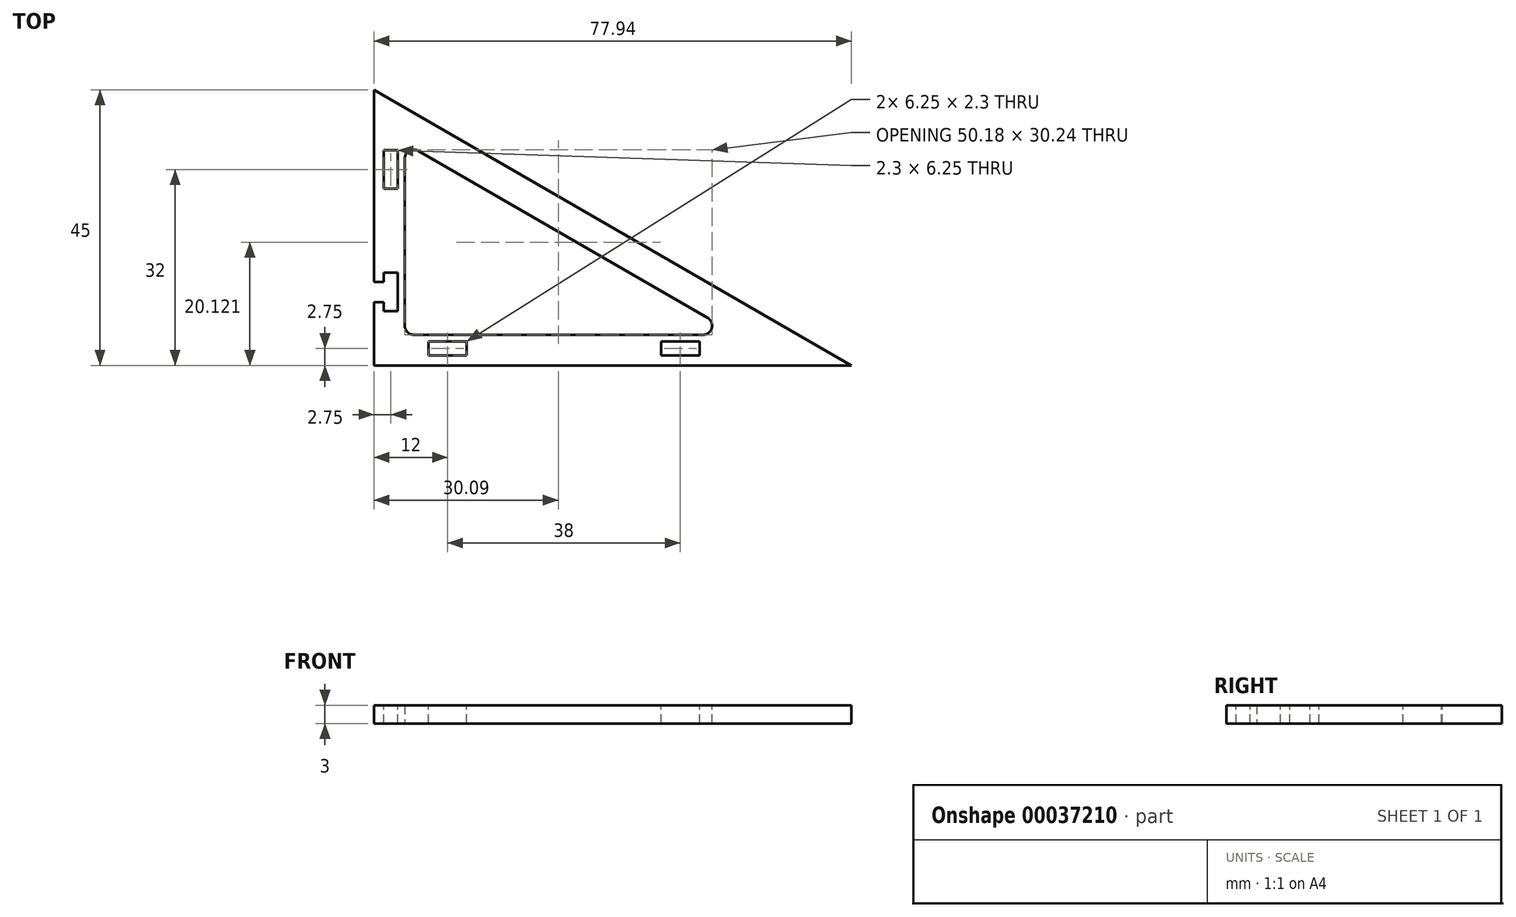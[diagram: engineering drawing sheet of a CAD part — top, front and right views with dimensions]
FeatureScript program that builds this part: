
annotation { "Feature Type Name" : "Feature", "Feature Type Description" : "" }
export const myFeature = defineFeature(function(context is Context, id is Id, definition is map)
    precondition{}
    {
        {
            var Q0;
            Q0=qCreatedBy(makeId("Top.planeOp"),FACE);
            var sketch = newSketch(context, id + "F0", { "sketchPlane" : qUnion([Q0])});
            skLineSegment(sketch, "E0", {"start": v(-30.01, 0) * mm, "end": v(47.93, 0) * mm});
            skLineSegment(sketch, "E1", {"start": v(-30.01, 0) * mm, "end": v(-30.01, 45) * mm});
            skLineSegment(sketch, "E2", {"start": v(-30.01, 45) * mm, "end": v(47.93, 0) * mm});
            skLineSegment(sketch, "E3", {"start": v(-25.01, 5) * mm, "end": v(-25.01, 36.34) * mm});
            skLineSegment(sketch, "E4", {"start": v(-25.01, 36.34) * mm, "end": v(29.27, 5) * mm});
            skLineSegment(sketch, "E5", {"start": v(29.27, 5) * mm, "end": v(-25.01, 5) * mm});
            skSolve(sketch);
        }
        {
            var Q0;
            Q0=makeQuery(id+"F0.imprint","IMPRINT",FACE,{"disambiguationData":[TD([[makeQuery(id+"F0.imprint","IMPRINT",EDGE,{"derivedFrom":sQuery(id+"F0.wireOp",EDGE,"E0")}),1.0]])]});
            extrude(context, id + "F1", {"entities" : qUnion([Q0]), "depth" : 3 * mm});
        }
        {
            var Q0;
            Q0=makeQuery(id+"F1.opExtrude","SWEPT_EDGE",EDGE,{"disambiguationData":[OSD([sQuery(id+"F0.wireOp",EDGE,"E3"),sQuery(id+"F0.wireOp",EDGE,"E4")])]});
            var Q1;
            Q1=makeQuery(id+"F1.opExtrude","SWEPT_EDGE",EDGE,{"disambiguationData":[OSD([sQuery(id+"F0.wireOp",EDGE,"E4"),sQuery(id+"F0.wireOp",EDGE,"E5")])]});
            var Q2;
            Q2=makeQuery(id+"F1.opExtrude","SWEPT_EDGE",EDGE,{"disambiguationData":[OSD([sQuery(id+"F0.wireOp",EDGE,"E3"),sQuery(id+"F0.wireOp",EDGE,"E5")])]});
            fillet(context, id + "F2", {"entities" : qUnion([Q0, Q1, Q2]), "radius" : 1.5 * mm, "tangentPropagation" : true, "allowEdgeOverflow" : false});
        }
        {
            var Q0;
            Q0=makeQuery(id+"F1.opExtrude","CAP_FACE",FACE,{"disambiguationData":[OSD([sQuery(id+"F0.wireOp",EDGE,"E0"),sQuery(id+"F0.wireOp",EDGE,"E1"),sQuery(id+"F0.wireOp",EDGE,"E2"),sQuery(id+"F0.wireOp",EDGE,"E3"),sQuery(id+"F0.wireOp",EDGE,"E4"),sQuery(id+"F0.wireOp",EDGE,"E5")])],"isStart":false});
            var sketch = newSketch(context, id + "F3", { "sketchPlane" : qUnion([Q0])});
            skLineSegment(sketch, "E6.rect.bottom", {"start": v(23.11, 1.6) * mm, "end": v(16.86, 1.6) * mm});
            skLineSegment(sketch, "E6.rect.top", {"start": v(23.11, 3.9) * mm, "end": v(16.86, 3.9) * mm});
            skLineSegment(sketch, "E6.rect.left", {"start": v(23.11, 1.6) * mm, "end": v(23.11, 3.9) * mm});
            skLineSegment(sketch, "E6.rect.right", {"start": v(16.86, 1.6) * mm, "end": v(16.86, 3.9) * mm});
            skPoint(sketch, "E6.rect.middle", {"position": v(19.99, 2.75) * mm});
            skLineSegment(sketch, "E7.rect.bottom", {"start": v(-14.89, 3.9) * mm, "end": v(-21.14, 3.9) * mm});
            skLineSegment(sketch, "E7.rect.top", {"start": v(-14.89, 1.6) * mm, "end": v(-21.14, 1.6) * mm});
            skLineSegment(sketch, "E7.rect.left", {"start": v(-14.89, 3.9) * mm, "end": v(-14.89, 1.6) * mm});
            skLineSegment(sketch, "E7.rect.right", {"start": v(-21.14, 3.9) * mm, "end": v(-21.14, 1.6) * mm});
            skPoint(sketch, "E7.rect.middle", {"position": v(-18.01, 2.75) * mm});
            skLineSegment(sketch, "E8.rect.bottom", {"start": v(-26.11, 28.88) * mm, "end": v(-28.41, 28.88) * mm});
            skLineSegment(sketch, "E8.rect.top", {"start": v(-26.11, 35.12) * mm, "end": v(-28.41, 35.12) * mm});
            skLineSegment(sketch, "E8.rect.left", {"start": v(-26.11, 28.88) * mm, "end": v(-26.11, 35.12) * mm});
            skLineSegment(sketch, "E8.rect.right", {"start": v(-28.41, 28.88) * mm, "end": v(-28.41, 35.12) * mm});
            skPoint(sketch, "E8.rect.middle", {"position": v(-27.26, 32) * mm});
            skLineSegment(sketch, "E9.rect.bottom", {"start": v(-26.11, 8.87) * mm, "end": v(-28.41, 8.87) * mm});
            skLineSegment(sketch, "E9.rect.top", {"start": v(-26.11, 15.12) * mm, "end": v(-28.41, 15.12) * mm});
            skLineSegment(sketch, "E9.rect.left", {"start": v(-26.11, 8.87) * mm, "end": v(-26.11, 15.12) * mm});
            skLineSegment(sketch, "E9.rect.right", {"start": v(-28.41, 8.87) * mm, "end": v(-28.41, 15.12) * mm});
            skPoint(sketch, "E9.rect.middle", {"position": v(-27.26, 12) * mm});
            skLineSegment(sketch, "E10.rect.bottom", {"start": v(21.64, 1.6) * mm, "end": v(18.34, 1.6) * mm});
            skLineSegment(sketch, "E10.rect.top", {"start": v(21.64, 0) * mm, "end": v(18.34, 0) * mm});
            skLineSegment(sketch, "E10.rect.left", {"start": v(21.64, 1.6) * mm, "end": v(21.64, 0) * mm});
            skLineSegment(sketch, "E10.rect.right", {"start": v(18.34, 1.6) * mm, "end": v(18.34, 0) * mm});
            skPoint(sketch, "E10.rect.middle", {"position": v(19.99, 0.8) * mm});
            skPoint(sketch, "E10.rect.middle.positionSnap0", {"position": v(19.99, 1.6) * mm});
            skPoint(sketch, "E10.rect.centerSnap0", {"position": v(19.99, 1.6) * mm});
            skLineSegment(sketch, "E11.rect.bottom", {"start": v(-16.36, 1.6) * mm, "end": v(-19.66, 1.6) * mm});
            skLineSegment(sketch, "E11.rect.top", {"start": v(-16.36, 0) * mm, "end": v(-19.66, 0) * mm});
            skLineSegment(sketch, "E11.rect.left", {"start": v(-16.36, 1.6) * mm, "end": v(-16.36, 0) * mm});
            skLineSegment(sketch, "E11.rect.right", {"start": v(-19.66, 1.6) * mm, "end": v(-19.66, 0) * mm});
            skPoint(sketch, "E11.rect.middle", {"position": v(-18.01, 0.8) * mm});
            skLineSegment(sketch, "E12.rect.bottom", {"start": v(-28.41, 13.65) * mm, "end": v(-30.01, 13.65) * mm});
            skLineSegment(sketch, "E12.rect.top", {"start": v(-28.41, 10.35) * mm, "end": v(-30.01, 10.35) * mm});
            skLineSegment(sketch, "E12.rect.left", {"start": v(-28.41, 13.65) * mm, "end": v(-28.41, 10.35) * mm});
            skLineSegment(sketch, "E12.rect.right", {"start": v(-30.01, 13.65) * mm, "end": v(-30.01, 10.35) * mm});
            skPoint(sketch, "E12.rect.middle", {"position": v(-29.21, 12) * mm});
            skLineSegment(sketch, "E13.rect.bottom", {"start": v(-28.41, 33.65) * mm, "end": v(-30.01, 33.65) * mm});
            skLineSegment(sketch, "E13.rect.top", {"start": v(-28.41, 30.35) * mm, "end": v(-30.01, 30.35) * mm});
            skLineSegment(sketch, "E13.rect.left", {"start": v(-28.41, 33.65) * mm, "end": v(-28.41, 30.35) * mm});
            skLineSegment(sketch, "E13.rect.right", {"start": v(-30.01, 33.65) * mm, "end": v(-30.01, 30.35) * mm});
            skPoint(sketch, "E13.rect.middle", {"position": v(-29.21, 32) * mm});
            skPoint(sketch, "E13.rect.middle.positionSnap0", {"position": v(-28.41, 32) * mm});
            skPoint(sketch, "E13.rect.centerSnap0", {"position": v(-28.41, 32) * mm});
            skLineSegment(sketch, "E14", {"start": v(-30.01, 42.11) * mm, "end": v(42.93, 0) * mm, "construction": true});
            skLineSegment(sketch, "E15", {"start": v(-27.06, 41.74) * mm, "end": v(-21.65, 38.61) * mm});
            skLineSegment(sketch, "E16", {"start": v(-22.8, 36.62) * mm, "end": v(-28.21, 39.75) * mm});
            skLineSegment(sketch, "E17", {"start": v(-27.06, 41.74) * mm, "end": v(-28.21, 39.75) * mm});
            skLineSegment(sketch, "E18", {"start": v(-21.65, 38.61) * mm, "end": v(-22.8, 36.62) * mm});
            skPoint(sketch, "E19", {"position": v(-27.64, 40.74) * mm});
            skPoint(sketch, "E20", {"position": v(-24.35, 40.18) * mm});
            skPoint(sketch, "E21", {"position": v(-23.51, 6.5) * mm});
            skPoint(sketch, "E22", {"position": v(-24.93, 39.18) * mm});
            skSolve(sketch);
        }
        {
            var Q0;
            Q0=makeQuery(id+"F3.imprint","IMPRINT",FACE,{"disambiguationData":[TD([[makeQuery(id+"F3.imprint","IMPRINT",EDGE,{"derivedFrom":sQuery(id+"F3.wireOp",EDGE,"E8.rect.bottom")}),-1.0]])]});
            var Q1;
            Q1=makeQuery(id+"F3.imprint","IMPRINT",FACE,{"disambiguationData":[TD([[makeQuery(id+"F3.imprint","IMPRINT",EDGE,{"derivedFrom":sQuery(id+"F3.wireOp",EDGE,"E9.rect.bottom")}),-1.0]])]});
            var Q2;
            Q2=makeQuery(id+"F3.imprint","IMPRINT",FACE,{"disambiguationData":[TD([[makeQuery(id+"F3.imprint","IMPRINT",EDGE,{"derivedFrom":sQuery(id+"F3.wireOp",EDGE,"E7.rect.bottom")}),1.0]])]});
            var Q3;
            Q3=makeQuery(id+"F3.imprint","IMPRINT",FACE,{"disambiguationData":[TD([[makeQuery(id+"F3.imprint","IMPRINT",EDGE,{"derivedFrom":sQuery(id+"F3.wireOp",EDGE,"E6.rect.bottom")}),-1.0]])]});
            var Q4;
            Q4=makeQuery(id+"F3.imprint","IMPRINT",FACE,{"disambiguationData":[TD([[makeQuery(id+"F3.imprint","IMPRINT",EDGE,{"derivedFrom":sQuery(id+"F3.wireOp",EDGE,"E10.rect.bottom")}),1.0]])]});
            var Q5;
            {var subQ5=sQuery(id+"F3.wireOp",EDGE,"E13.rect.left");Q5=makeQuery(id+"F3.imprint","IMPRINT",FACE,{"disambiguationData":[TD([[makeQuery(id+"F3.imprint","IMPRINT",EDGE,{"derivedFrom":subQ5}),-1.0]])]});}
            var Q6;
            Q6=makeQuery(id+"F3.imprint","IMPRINT",FACE,{"disambiguationData":[TD([[makeQuery(id+"F3.imprint","IMPRINT",EDGE,{"derivedFrom":sQuery(id+"F3.wireOp",EDGE,"E11.rect.bottom")}),1.0]])]});
            var Q7;
            Q7=makeQuery(id+"F3.imprint","IMPRINT",FACE,{"disambiguationData":[TD([[makeQuery(id+"F3.imprint","IMPRINT",EDGE,{"derivedFrom":sQuery(id+"F3.wireOp",EDGE,"E12.rect.bottom")}),1.0]])]});
            extrude(context, id + "F4", {"entities" : qUnion([Q0, Q1, Q2, Q3, Q4, Q5, Q6, Q7]), "operationType" : NewBodyOperationType.REMOVE, "endBound" : BoundingType.THROUGH_ALL, "oppositeDirection" : true, "depth" : 25 * mm});
        }
    });
